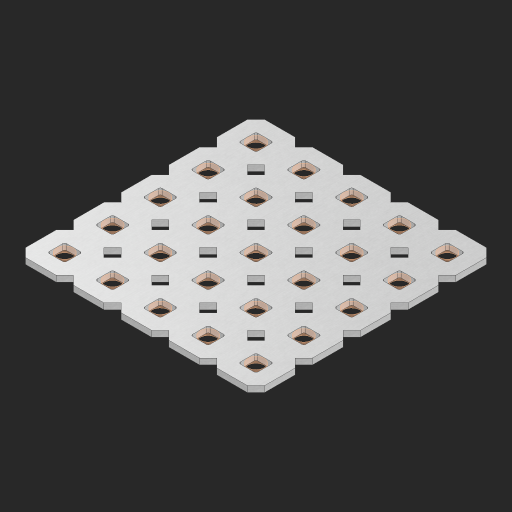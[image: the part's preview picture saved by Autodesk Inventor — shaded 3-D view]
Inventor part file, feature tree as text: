
AUTODESK INVENTOR PART (.ipt)
format: ipt  version: 2023 (Build 270158000, 158)  size: 588,288 bytes
history: native  units: in
note: dims shown in document units (in); Inventor stores cm internally (conversion verified against a paired STEP export)
features: other x26, extrude x24, sketch x2, pattern_linear x1
ambient origin geometry x8: Origin, YZ Plane, XZ Plane, XY Plane, X Axis, Y Axis, Z Axis, Center Point
bodies: Solid1 (feature_tree), Body (feature_tree)
feature tree (53):
  pattern_linear  "Rectangular Pattern1"  Spacing1=0.09in  [1 undecoded]
  sketch  "Sketch1"  dims[d1=0.5in]
  sketch  "Sketch2"  dims[d2=0.182in d3=0.09in d4=0.09in d5=0.09in d6=0.09in d7=0.09in d8=0.09in d9=0.09in d10=0.09in d11=0.02in d13=0.0in d14=0.172in d15=0.0625in d16=0.0in d19=0.5in d22=0.5in]
  other  "Srf1"
  other  "Srf126"
  other  "Srf127"
  other  "Srf128"
  other  "Srf129"
  other  "Srf268"
  other  "Srf269"
  other  "Srf270"
  other  "Srf271"
  other  "Srf272"
  other  "Srf293"
  other  "Srf294"
  other  "Srf295"
  other  "Srf296"
  other  "Srf297"
  other  "Srf318"
  other  "Srf319"
  other  "Srf320"
  other  "Srf321"
  other  "Srf322"
  other  "Srf343"
  other  "Srf344"
  other  "Srf345"
  other  "Srf346"
  other  "Srf347"
  other  "Circle"
  extrude  "ExtrusionSrf126"  Depth=0.09in
  extrude  "ExtrusionSrf127"  Depth=0.09in
  extrude  "ExtrusionSrf128"  Depth=0.09in
  extrude  "ExtrusionSrf129"  Depth=0.09in
  extrude  "ExtrusionSrf268"  Depth=0.09in
  extrude  "ExtrusionSrf269"  Depth=0.09in
  extrude  "ExtrusionSrf270"  Depth=0.09in
  extrude  "ExtrusionSrf271"  Depth=0.02in
  extrude  "ExtrusionSrf272"  TaperAngle=0.0deg  [1 undecoded]
  extrude  "ExtrusionSrf293"  Depth=0.5in
  extrude  "ExtrusionSrf294"  Depth=0.0625in TaperAngle=0.0deg
  extrude  "ExtrusionSrf295"  Depth=0.5in
  extrude  "ExtrusionSrf296"  Depth=0.5in
  extrude  "ExtrusionSrf297"  [1 undecoded]
  extrude  "ExtrusionSrf318"  [1 undecoded]
  extrude  "ExtrusionSrf319"  [1 undecoded]
  extrude  "ExtrusionSrf320"  [1 undecoded]
  extrude  "ExtrusionSrf321"  [1 undecoded]
  extrude  "ExtrusionSrf322"  [1 undecoded]
  extrude  "ExtrusionSrf343"  [1 undecoded]
  extrude  "ExtrusionSrf344"  [1 undecoded]
  extrude  "ExtrusionSrf345"  [1 undecoded]
  extrude  "ExtrusionSrf346"  [1 undecoded]
  extrude  "ExtrusionSrf347"  [1 undecoded]
note: 13 required parameter values undecoded (feature->parameter linkage not recoverable at this tier; creation-order binding heuristic only, values carry confidence <= 0.55)
